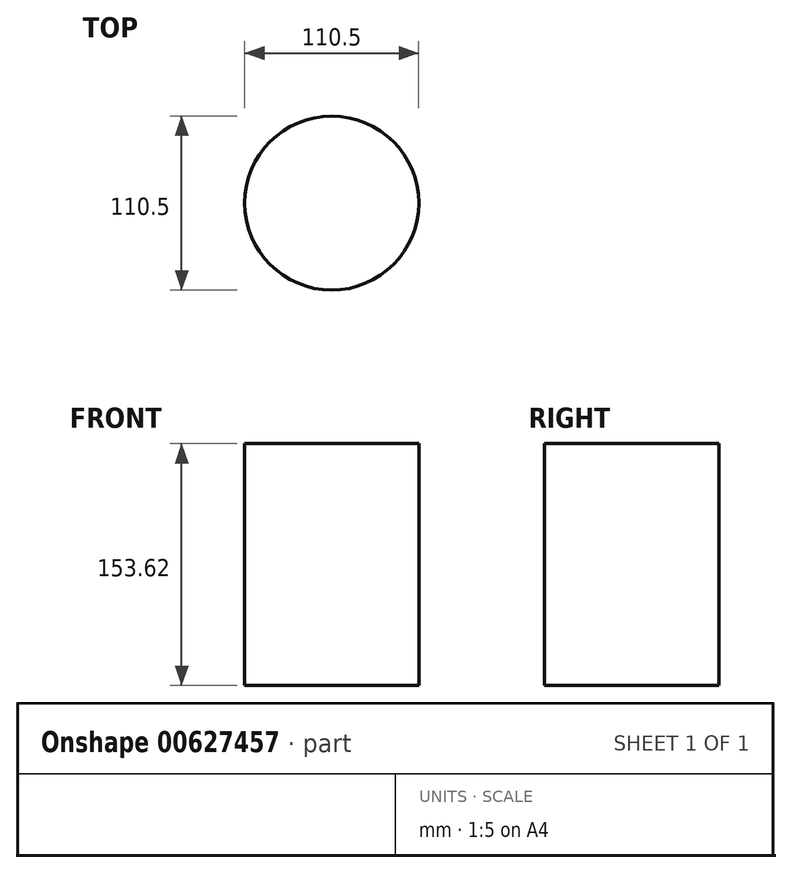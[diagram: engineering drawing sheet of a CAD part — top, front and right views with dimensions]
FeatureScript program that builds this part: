
annotation { "Feature Type Name" : "Feature", "Feature Type Description" : "" }
export const myFeature = defineFeature(function(context is Context, id is Id, definition is map)
    precondition{}
    {
        {
            var Q0;
            Q0=qCreatedBy(makeId("Top.planeOp"),FACE);
            var sketch = newSketch(context, id + "F0", { "sketchPlane" : qUnion([Q0])});
            skCircle(sketch, "E0", {"center": v(0, 0) * mm, "radius": 55.25 * mm});
            skSolve(sketch);
        }
        {
            var Q0;
            Q0 = qSketchRegion(id + "F0", true);
            extrude(context, id + "F1", {"entities" : qUnion([Q0]), "depth" : 153.62 * mm, "offsetDistance" : 25.4 * mm});
        }
    });
